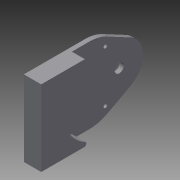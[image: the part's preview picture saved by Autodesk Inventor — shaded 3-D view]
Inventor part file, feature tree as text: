
AUTODESK INVENTOR PART (.ipt)
format: ipt  version: 2015 (Build 190159000, 159)  size: 110,080 bytes
history: native  units: mm
features: extrude x2, sketch x2, fillet x1
ambient origin geometry x8: Origin, YZ Plane, XZ Plane, XY Plane, X Axis, Y Axis, Z Axis, Center Point
bodies: Body1 (feature_tree)
feature tree (5):
  extrude  "Extrusion3"  Depth=8.5mm
  extrude  "Extrusion4"  Depth=2.0mm
  fillet  "Fillet1"  Radius=12.7mm
  sketch  "Sketch3"  dims[d4=32.0mm d9=50.0mm d27=44.0mm d28=44.0mm d31=8.5mm]
  sketch  "Sketch4"  dims[d32=44.0mm d33=27.64mm d35=12.7mm d36=23.82mm d37=23.82mm d38=3.5mm d40=3.5mm d41=84.0mm d42=16.0mm d43=0.0mm d44=27.64mm d45=12.0mm d46=0.0mm d47=2.0mm]
